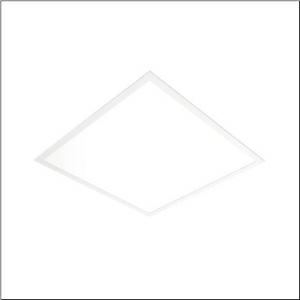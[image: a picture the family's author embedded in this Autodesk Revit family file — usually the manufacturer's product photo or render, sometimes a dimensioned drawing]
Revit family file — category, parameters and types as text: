
# Revit family: apollon_r__41_51mh12wm2m43_c8ca
name_source: partatom
category: Lighting Fixtures
units: mm (PartAtom-declared; Revit-internal decimal feet)

## family parameters
Cut with Voids When Loaded = No
Host = Face
Light Source = No
Part Type = Normal
Room Calculation Point = No
Round Connector Dimension = Use Diameter
Shared = No

## types (1)
- --- (1 x LED, 4380 lm, 35 W, 4000K)
    Apparent Load = 35 VA
    CIE Flux Codes = 61 87 97 100 100
    Color Rendering = 80
    Color Temperature = 4000K
    Default Elevation = 1800 mm
    Description = Apollon® 41, office luminaire, primary optical cover: prismatic diffuser, of PS, light emission: direct distribution, primary light characteristic: symmetric, installation type: lay-in mounting, LED, rated luminous flux: 4.375lm, luminous efficacy: 125lm/W, light colour: 830/840, colour temperature: 3000/4000K, control gear: ON/OFF Multilumen, with terminal, 3-pole, mains connection: 220..240V, AC, 50/60Hz, rated input power: 35W, housing, of aluminium section, traffic white (RAL 9016), module: M600, length: 595mm, width: 595mm, height: 60mm, recess depth: 180mm, housing upper side, of sheet steel, protection rating (complete): IP20, protection rating (lamp compartment, on room side): IP40, insulation class (complete): insulation class II (safety insulation), certification: CE, ENEC, impact resistance: IK03, permissible operating ambient temperature: -25..+40°C, packaging unit: 1 piece
    Height = 0 mm  [stored 0 ft]
    Lamp = 1 x LED
    Lamp Light Flux = 4380 lm
    Lamp Power = 35 W
    Lamp count = 1
    Length = 600 mm
    Luminous efficacy = 125 lm/W
    Manufacturer = Siteco
    ModVariant = No
    Model = 51MH12WM2M43
    Mounting Place = Ceiling
    Mounting Type = Recessed
    Number of Poles = 1
    OnlyDefault = Yes
    Power Factor = 1
    Product Name = Apollon® 41
    Product group = office luminaire | ceiling recessed
    ProductGroupID = 400
    Protection Class = Protection class II
    Protection Degree = IP 20
    RLX_Detail_Level = 1
    RLX_Emergency_Light_Flux = 0 lm
    RLX_Emergency_Type = 0
    RLX_Emergency_Type_DB = No
    RlxData = <blob elided: 13589 chars, md5=c92d494f>
    Socket = socket
    Standby Power = 0 W
    System Light Flux = 4380 lm
    System Power = 35 W
    Type Comments = factory setting: luminous flux: 100 % | (ON | ON) | 900 mA
    Type Image = l_1291024.jpg
    URL = http://relux.com
    VarID = @adj_033623
    Voltage = 0 V
    Weight = 0.00 kg
    Width = 600 mm

note: [stored X ft] marks values corroborated as IEEE doubles in the binary element streams (Revit-internal decimal feet)

## geometry (parser evidence)
native form markers: Sweep x10
no freeform markers — native parametric forms only
